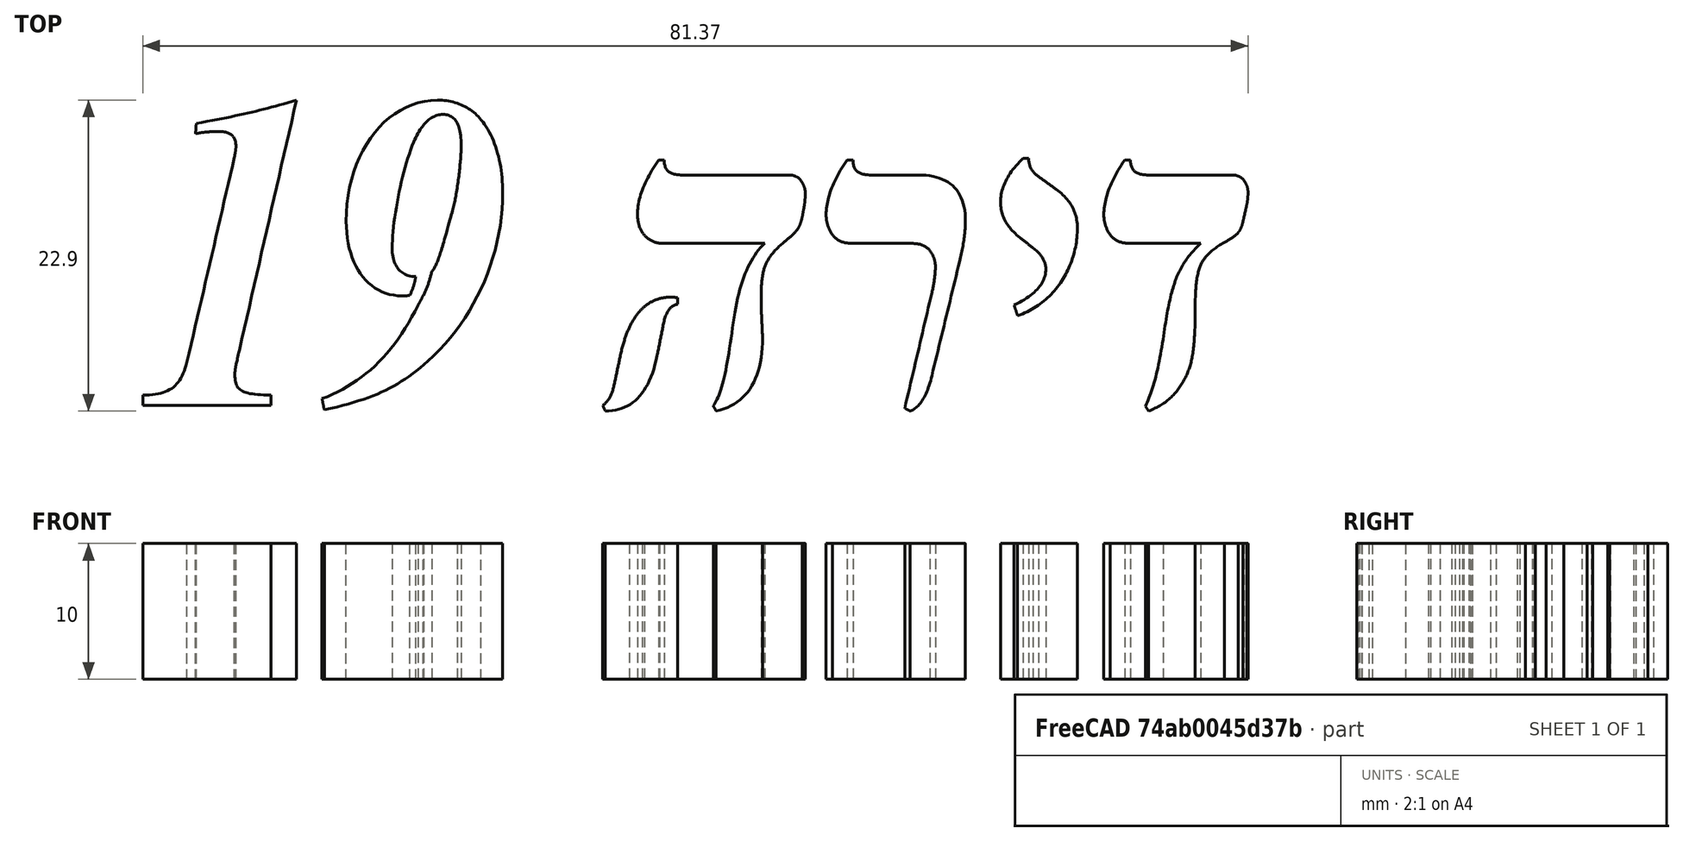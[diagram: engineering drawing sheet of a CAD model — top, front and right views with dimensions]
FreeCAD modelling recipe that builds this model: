
FCSTD DOCUMENT  (FreeCAD 0.18R16110 (Git))
Label: dira1
License: All rights reserved
LicenseURL: http://en.wikipedia.org/wiki/All_rights_reserved
objects: Part::Feature×10, Part::Extrusion×9, Part::Cut×3
note: 22 computed .brp shape members not serialized (recipe doc carries the construction recipe); baked Part::Feature solids carry a one-line shape summary decoded from their .brp

FEATURE [Part::Feature] path2019
  shape: bbox 11.31 x 22.48 x 2.195e-07 mm, 0 faces, 0 solids (baked)
FEATURE [Part::Feature] path2021
  shape: bbox 13.3 x 22.81 x 2.195e-07 mm, 0 faces, 0 solids (baked)
FEATURE [Part::Feature] path2021001
  shape: bbox 5.081 x 11.95 x 2.195e-07 mm, 0 faces, 0 solids (baked)
FEATURE [Part::Feature] path2023
  shape: bbox 10.62 x 18.48 x 2.195e-07 mm, 0 faces, 0 solids (baked)
FEATURE [Part::Feature] path2025
  shape: bbox 5.655 x 11.62 x 2.195e-07 mm, 0 faces, 0 solids (baked)
FEATURE [Part::Feature] path2027
  shape: bbox 10.26 x 18.48 x 2.195e-07 mm, 0 faces, 0 solids (baked)
FEATURE [Part::Feature] path2029
  shape: bbox 12.35 x 18.48 x 2.195e-07 mm, 0 faces, 0 solids (baked)
FEATURE [Part::Feature] path2029001
  shape: bbox 5.508 x 8.42 x 2.195e-07 mm, 0 faces, 0 solids (baked)
FEATURE [Part::Extrusion] Extrude  label="uno"
  Base = -> path2019
  Dir = (0,0,1)
  DirMode = 2
  FaceMakerClass = Part::FaceMakerBullseye
  LengthFwd = 10
  LengthRev = 0
  Placement = pos=(0,0,-10) rot=(0,0,1;0rad)
  Solid = true
  Symmetric = false
FEATURE [Part::Extrusion] Extrude001  label="nueve_maciso"
  Base = -> path2021
  Dir = (0,0,1)
  DirMode = 2
  FaceMakerClass = Part::FaceMakerBullseye
  LengthFwd = 10
  LengthRev = 0
  Placement = pos=(0,0,-10) rot=(0,0,1;0rad)
  Solid = true
  Symmetric = false
FEATURE [Part::Extrusion] Extrude002  label="nueve_interno"
  Base = -> path2021001
  Dir = (0,0,-1)
  DirMode = 2
  FaceMakerClass = Part::FaceMakerBullseye
  LengthFwd = 10
  LengthRev = 0
  Solid = true
  Symmetric = false
FEATURE [Part::Extrusion] Extrude003  label="dalet"
  Base = -> path2023
  Dir = (0,0,-1)
  DirMode = 2
  FaceMakerClass = Part::FaceMakerBullseye
  LengthFwd = 10
  LengthRev = 0
  Solid = true
  Symmetric = false
FEATURE [Part::Extrusion] Extrude004  label="yud"
  Base = -> path2025
  Dir = (0,0,-1)
  DirMode = 2
  FaceMakerClass = Part::FaceMakerBullseye
  LengthFwd = 10
  LengthRev = 0
  Solid = true
  Symmetric = false
FEATURE [Part::Extrusion] Extrude005  label="reish"
  Base = -> path2027
  Dir = (0,0,-1)
  DirMode = 2
  FaceMakerClass = Part::FaceMakerBullseye
  LengthFwd = 10
  LengthRev = 0
  Solid = true
  Symmetric = false
FEATURE [Part::Extrusion] Extrude006  label="hey-1"
  Base = -> path2029
  Dir = (0,0,-1)
  DirMode = 2
  FaceMakerClass = Part::FaceMakerBullseye
  LengthFwd = 10
  LengthRev = 0
  Solid = true
  Symmetric = false
FEATURE [Part::Extrusion] Extrude014
  Base = -> path2029
  Dir = (0,0,-1)
  DirMode = 2
  FaceMakerClass = Part::FaceMakerBullseye
  LengthFwd = 10
  LengthRev = 0
  Solid = true
  Symmetric = false
FEATURE [Part::Extrusion] Extrude015  label="hey-2"
  Base = -> path2029001
  Dir = (0,0,-1)
  DirMode = 2
  FaceMakerClass = Part::FaceMakerBullseye
  LengthFwd = 10
  LengthRev = 0
  Solid = true
  Symmetric = false
FEATURE [Part::Cut] Cut  label="nueve"
  Base = -> Extrude001
  Tool = -> Extrude002
FEATURE [Part::Feature] Cut001001  label="Cut002"
  Placement = pos=(-57.761,-21.7429,0) rot=(0,0,-1;5.67232rad)
  shape: bbox 1.943 x 5.366 x 10 mm, 8 faces (baked)
FEATURE [Part::Feature] Cut001002  label="Cut003"
  Placement = pos=(-56.0036,-31.9817,0) rot=(0,0,-1;5.53269rad)
  shape: bbox 1.968 x 5.453 x 10 mm, 8 faces (baked)
FEATURE [Part::Cut] Cut001003
  Base = -> Cut
  Tool = -> Cut001001
FEATURE [Part::Cut] Cut001004  label="nueve-con-corte"
  Base = -> Cut001003
  Tool = -> Cut001002
